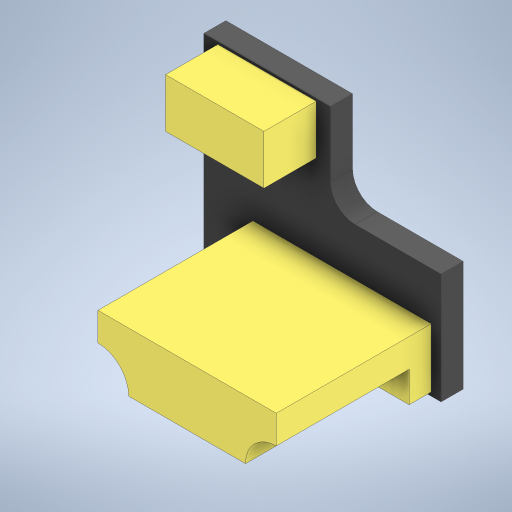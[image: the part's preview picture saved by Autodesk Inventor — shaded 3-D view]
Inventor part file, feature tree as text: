
AUTODESK INVENTOR PART (.ipt)
format: ipt  version: 2023.1 (Build 271208000, 208)  size: 279,552 bytes
history: native  units: mm
features: extrude x4, sketch x3, other x1, fillet x1
ambient origin geometry x8: Origin, YZ Plane, XZ Plane, XY Plane, X Axis, Y Axis, Z Axis, Center Point
bodies: Body1 (feature_tree)
feature tree (9):
  other  "솔리드1"
  extrude  "돌출1"  Depth=9.0mm
  fillet  "모깎기1"  Radius=19.3mm
  sketch  "스케치2"
  extrude  "돌출2"  Depth=16.3mm
  extrude  "돌출3"  Depth=10.3mm
  extrude  "돌출4"  Depth=1.8mm TaperAngle=0.0deg
  sketch  "스케치1"
  sketch  "스케치3"
